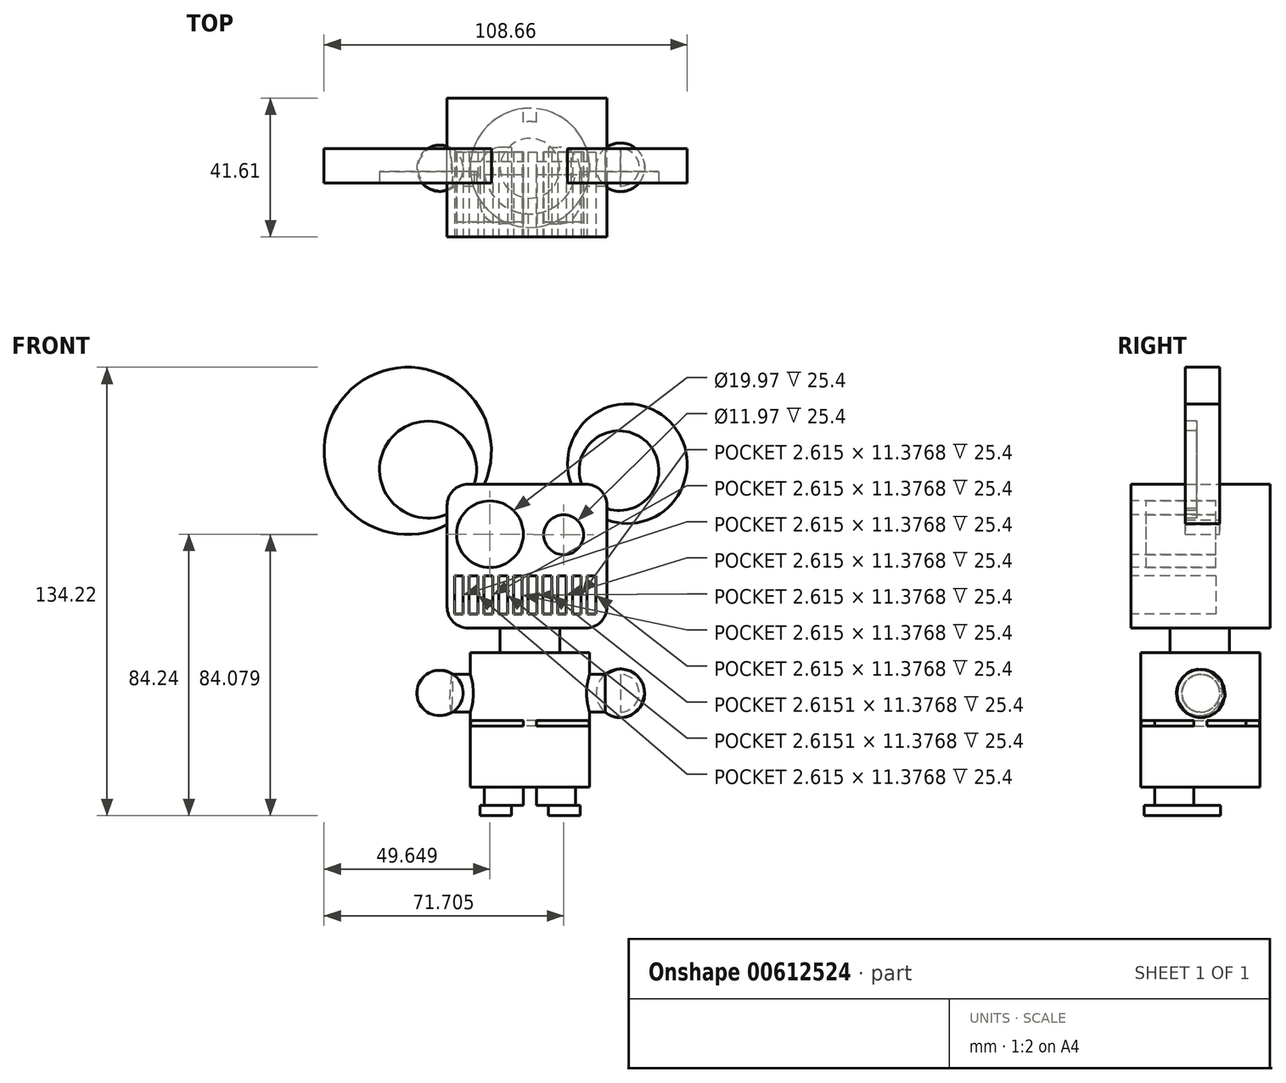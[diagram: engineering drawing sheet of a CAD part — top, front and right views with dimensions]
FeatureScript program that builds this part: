
annotation { "Feature Type Name" : "Feature", "Feature Type Description" : "" }
export const myFeature = defineFeature(function(context is Context, id is Id, definition is map)
    precondition{}
    {
        {
            var Q0;
            Q0=qCreatedBy(makeId("Front.planeOp"),FACE);
            var sketch = newSketch(context, id + "F0", { "sketchPlane" : qUnion([Q0])});
            skLineSegment(sketch, "E0.bottom", {"start": v(-18.42, 27.46) * mm, "end": v(16.7, 27.46) * mm});
            skLineSegment(sketch, "E0.top", {"start": v(-18.42, -15.66) * mm, "end": v(16.7, -15.66) * mm});
            skLineSegment(sketch, "E0.left", {"start": v(-24.77, 21.1) * mm, "end": v(-24.77, -9.3) * mm});
            skLineSegment(sketch, "E0.right", {"start": v(23.04, 21.1) * mm, "end": v(23.04, -9.3) * mm});
            skPoint(sketch, "E1.visualSharp", {"position": v(23.04, 27.46) * mm});
            skArc(sketch, "E1.filletArc", {"start": v(23.04, 21.1) * mm, "mid": v(21.18, 25.6) * mm, "end": v(16.7, 27.46) * mm});
            skPoint(sketch, "E2.visualSharp", {"position": v(23.04, -15.66) * mm});
            skArc(sketch, "E2.filletArc", {"start": v(16.7, -15.66) * mm, "mid": v(21.18, -13.8) * mm, "end": v(23.04, -9.3) * mm});
            skPoint(sketch, "E3.visualSharp", {"position": v(-24.77, 27.46) * mm});
            skArc(sketch, "E3.filletArc", {"start": v(-18.42, 27.46) * mm, "mid": v(-22.9, 25.6) * mm, "end": v(-24.77, 21.1) * mm});
            skPoint(sketch, "E4.visualSharp", {"position": v(-24.77, -15.66) * mm});
            skArc(sketch, "E4.filletArc", {"start": v(-24.77, -9.3) * mm, "mid": v(-22.9, -13.8) * mm, "end": v(-18.42, -15.66) * mm});
            skSolve(sketch);
        }
        {
            var Q0;
            Q0 = qSketchRegion(id + "F0", true);
            extrude(context, id + "F1", {"entities" : qUnion([Q0]), "depth" : 41.6 * mm, "offsetDistance" : 25.4 * mm});
        }
        {
            var Q0;
            Q0=makeQuery(id+"F1.opExtrude","CAP_FACE",FACE,{"disambiguationData":[OSD([sQuery(id+"F0.wireOp",EDGE,"E0.bottom"),sQuery(id+"F0.wireOp",EDGE,"E0.top"),sQuery(id+"F0.wireOp",EDGE,"E0.left"),sQuery(id+"F0.wireOp",EDGE,"E0.right"),sQuery(id+"F0.wireOp",EDGE,"E1.filletArc"),sQuery(id+"F0.wireOp",EDGE,"E2.filletArc"),sQuery(id+"F0.wireOp",EDGE,"E3.filletArc"),sQuery(id+"F0.wireOp",EDGE,"E4.filletArc")])],"isStart":false});
            var sketch = newSketch(context, id + "F2", { "sketchPlane" : qUnion([Q0])});
            skCircle(sketch, "E5", {"center": v(-11.95, 12.46) * mm, "radius": 9.98 * mm});
            skSolve(sketch);
        }
        {
            var Q0;
            Q0 = qSketchRegion(id + "F2", true);
            extrude(context, id + "F3", {"entities" : qUnion([Q0]), "operationType" : NewBodyOperationType.REMOVE, "oppositeDirection" : true, "depth" : 25.4 * mm, "offsetDistance" : 25.4 * mm});
        }
        {
            var Q0;
            Q0=makeQuery(id+"F1.opExtrude","CAP_FACE",FACE,{"disambiguationData":[OSD([sQuery(id+"F0.wireOp",EDGE,"E0.bottom"),sQuery(id+"F0.wireOp",EDGE,"E0.top"),sQuery(id+"F0.wireOp",EDGE,"E0.left"),sQuery(id+"F0.wireOp",EDGE,"E0.right"),sQuery(id+"F0.wireOp",EDGE,"E1.filletArc"),sQuery(id+"F0.wireOp",EDGE,"E2.filletArc"),sQuery(id+"F0.wireOp",EDGE,"E3.filletArc"),sQuery(id+"F0.wireOp",EDGE,"E4.filletArc")])],"isStart":false});
            var sketch = newSketch(context, id + "F4", { "sketchPlane" : qUnion([Q0])});
            skCircle(sketch, "E6", {"center": v(10.1, 12.3) * mm, "radius": 5.99 * mm});
            skSolve(sketch);
        }
        {
            var Q0;
            Q0 = qSketchRegion(id + "F4", true);
            extrude(context, id + "F5", {"entities" : qUnion([Q0]), "operationType" : NewBodyOperationType.REMOVE, "oppositeDirection" : true, "depth" : 25.4 * mm, "offsetDistance" : 25.4 * mm});
        }
        {
            var Q0;
            Q0=makeQuery(id+"F3.boolean.opBoolean","COPY",FACE,{"derivedFrom":makeQuery(id+"F3.opExtrude","CAP_FACE",FACE,{"disambiguationData":[OSD([sQuery(id+"F2.wireOp",EDGE,"E5")])],"isStart":false})});
            var Q1;
            Q1=makeQuery(id+"F5.boolean.opBoolean","COPY",FACE,{"derivedFrom":makeQuery(id+"F5.opExtrude","CAP_FACE",FACE,{"disambiguationData":[OSD([sQuery(id+"F4.wireOp",EDGE,"E6")])],"isStart":false})});
            extrude(context, id + "F6", {"entities" : qUnion([Q0, Q1]), "depth" : 20.91 * mm, "offsetDistance" : 25.4 * mm});
        }
        {
            var Q0;
            Q0=makeQuery(id+"F1.opExtrude","CAP_FACE",FACE,{"disambiguationData":[OSD([sQuery(id+"F0.wireOp",EDGE,"E0.bottom"),sQuery(id+"F0.wireOp",EDGE,"E0.top"),sQuery(id+"F0.wireOp",EDGE,"E0.left"),sQuery(id+"F0.wireOp",EDGE,"E0.right"),sQuery(id+"F0.wireOp",EDGE,"E1.filletArc"),sQuery(id+"F0.wireOp",EDGE,"E2.filletArc"),sQuery(id+"F0.wireOp",EDGE,"E3.filletArc"),sQuery(id+"F0.wireOp",EDGE,"E4.filletArc")])],"isStart":false});
            var sketch = newSketch(context, id + "F7", { "sketchPlane" : qUnion([Q0])});
            skLineSegment(sketch, "E7.bottom", {"start": v(-22.58, 0) * mm, "end": v(-19.97, 0) * mm});
            skLineSegment(sketch, "E7.top", {"start": v(-22.58, -11.38) * mm, "end": v(-19.97, -11.38) * mm});
            skLineSegment(sketch, "E7.left", {"start": v(-22.58, 0) * mm, "end": v(-22.58, -11.38) * mm});
            skLineSegment(sketch, "E7.right", {"start": v(-19.97, 0) * mm, "end": v(-19.97, -11.38) * mm});
            skLineSegment(sketch, "E8.1.0.0", {"start": v(-18.17, 0) * mm, "end": v(-15.55, 0) * mm});
            skLineSegment(sketch, "E8.1.0.1", {"start": v(-15.55, 0) * mm, "end": v(-15.55, -11.38) * mm});
            skLineSegment(sketch, "E8.1.0.2", {"start": v(-18.17, 0) * mm, "end": v(-18.17, -11.38) * mm});
            skLineSegment(sketch, "E8.1.0.3", {"start": v(-18.17, -11.38) * mm, "end": v(-15.55, -11.38) * mm});
            skLineSegment(sketch, "E8.2.0.0", {"start": v(-13.76, 0) * mm, "end": v(-11.14, 0) * mm});
            skLineSegment(sketch, "E8.2.0.1", {"start": v(-11.14, 0) * mm, "end": v(-11.14, -11.38) * mm});
            skLineSegment(sketch, "E8.2.0.2", {"start": v(-13.76, 0) * mm, "end": v(-13.76, -11.38) * mm});
            skLineSegment(sketch, "E8.2.0.3", {"start": v(-13.76, -11.38) * mm, "end": v(-11.14, -11.38) * mm});
            skLineSegment(sketch, "E8.3.0.0", {"start": v(-9.34, 0) * mm, "end": v(-6.73, 0) * mm});
            skLineSegment(sketch, "E8.3.0.1", {"start": v(-6.73, 0) * mm, "end": v(-6.73, -11.38) * mm});
            skLineSegment(sketch, "E8.3.0.2", {"start": v(-9.34, 0) * mm, "end": v(-9.34, -11.38) * mm});
            skLineSegment(sketch, "E8.3.0.3", {"start": v(-9.34, -11.38) * mm, "end": v(-6.73, -11.38) * mm});
            skLineSegment(sketch, "E8.4.0.0", {"start": v(-4.93, 0) * mm, "end": v(-2.32, 0) * mm});
            skLineSegment(sketch, "E8.4.0.1", {"start": v(-2.32, 0) * mm, "end": v(-2.32, -11.38) * mm});
            skLineSegment(sketch, "E8.4.0.2", {"start": v(-4.93, 0) * mm, "end": v(-4.93, -11.38) * mm});
            skLineSegment(sketch, "E8.4.0.3", {"start": v(-4.93, -11.38) * mm, "end": v(-2.32, -11.38) * mm});
            skLineSegment(sketch, "E8.5.0.0", {"start": v(-0.52, 0) * mm, "end": v(2.1, 0) * mm});
            skLineSegment(sketch, "E8.5.0.1", {"start": v(2.1, 0) * mm, "end": v(2.1, -11.38) * mm});
            skLineSegment(sketch, "E8.5.0.2", {"start": v(-0.52, 0) * mm, "end": v(-0.52, -11.38) * mm});
            skLineSegment(sketch, "E8.5.0.3", {"start": v(-0.52, -11.38) * mm, "end": v(2.1, -11.38) * mm});
            skLineSegment(sketch, "E8.6.0.0", {"start": v(3.9, 0) * mm, "end": v(6.5, 0) * mm});
            skLineSegment(sketch, "E8.6.0.1", {"start": v(6.5, 0) * mm, "end": v(6.5, -11.38) * mm});
            skLineSegment(sketch, "E8.6.0.2", {"start": v(3.9, 0) * mm, "end": v(3.9, -11.38) * mm});
            skLineSegment(sketch, "E8.6.0.3", {"start": v(3.9, -11.38) * mm, "end": v(6.5, -11.38) * mm});
            skLineSegment(sketch, "E8.7.0.0", {"start": v(8.3, 0) * mm, "end": v(10.92, 0) * mm});
            skLineSegment(sketch, "E8.7.0.1", {"start": v(10.92, 0) * mm, "end": v(10.92, -11.38) * mm});
            skLineSegment(sketch, "E8.7.0.2", {"start": v(8.3, 0) * mm, "end": v(8.3, -11.38) * mm});
            skLineSegment(sketch, "E8.7.0.3", {"start": v(8.3, -11.38) * mm, "end": v(10.92, -11.38) * mm});
            skLineSegment(sketch, "E8.8.0.0", {"start": v(12.72, 0) * mm, "end": v(15.33, 0) * mm});
            skLineSegment(sketch, "E8.8.0.1", {"start": v(15.33, 0) * mm, "end": v(15.33, -11.38) * mm});
            skLineSegment(sketch, "E8.8.0.2", {"start": v(12.72, 0) * mm, "end": v(12.72, -11.38) * mm});
            skLineSegment(sketch, "E8.8.0.3", {"start": v(12.72, -11.38) * mm, "end": v(15.33, -11.38) * mm});
            skLineSegment(sketch, "E8.9.0.0", {"start": v(17.13, 0) * mm, "end": v(19.74, 0) * mm});
            skLineSegment(sketch, "E8.9.0.1", {"start": v(19.74, 0) * mm, "end": v(19.74, -11.38) * mm});
            skLineSegment(sketch, "E8.9.0.2", {"start": v(17.13, 0) * mm, "end": v(17.13, -11.38) * mm});
            skLineSegment(sketch, "E8.9.0.3", {"start": v(17.13, -11.38) * mm, "end": v(19.74, -11.38) * mm});
            skLineSegment(sketch, "E8.direction1", {"start": v(-22.58, -11.38) * mm, "end": v(-18.17, -11.38) * mm, "construction": true});
            skSolve(sketch);
        }
        {
            var Q0;
            Q0=makeQuery(id+"F7.imprint","IMPRINT",FACE,{"disambiguationData":[TD([[makeQuery(id+"F7.imprint","IMPRINT",EDGE,{"derivedFrom":sQuery(id+"F7.wireOp",EDGE,"E8.8.0.0")}),-1.0]])]});
            var Q1;
            Q1=makeQuery(id+"F7.imprint","IMPRINT",FACE,{"disambiguationData":[TD([[makeQuery(id+"F7.imprint","IMPRINT",EDGE,{"derivedFrom":sQuery(id+"F7.wireOp",EDGE,"E8.4.0.0")}),-1.0]])]});
            var Q2;
            Q2=makeQuery(id+"F7.imprint","IMPRINT",FACE,{"disambiguationData":[TD([[makeQuery(id+"F7.imprint","IMPRINT",EDGE,{"derivedFrom":sQuery(id+"F7.wireOp",EDGE,"E8.5.0.0")}),-1.0]])]});
            var Q3;
            Q3=makeQuery(id+"F7.imprint","IMPRINT",FACE,{"disambiguationData":[TD([[makeQuery(id+"F7.imprint","IMPRINT",EDGE,{"derivedFrom":sQuery(id+"F7.wireOp",EDGE,"E8.7.0.0")}),-1.0]])]});
            var Q4;
            Q4=makeQuery(id+"F7.imprint","IMPRINT",FACE,{"disambiguationData":[TD([[makeQuery(id+"F7.imprint","IMPRINT",EDGE,{"derivedFrom":sQuery(id+"F7.wireOp",EDGE,"E7.bottom")}),-1.0]])]});
            var Q5;
            Q5=makeQuery(id+"F7.imprint","IMPRINT",FACE,{"disambiguationData":[TD([[makeQuery(id+"F7.imprint","IMPRINT",EDGE,{"derivedFrom":sQuery(id+"F7.wireOp",EDGE,"E8.9.0.0")}),-1.0]])]});
            var Q6;
            Q6=makeQuery(id+"F7.imprint","IMPRINT",FACE,{"disambiguationData":[TD([[makeQuery(id+"F7.imprint","IMPRINT",EDGE,{"derivedFrom":sQuery(id+"F7.wireOp",EDGE,"E8.6.0.0")}),-1.0]])]});
            var Q7;
            Q7=makeQuery(id+"F7.imprint","IMPRINT",FACE,{"disambiguationData":[TD([[makeQuery(id+"F7.imprint","IMPRINT",EDGE,{"derivedFrom":sQuery(id+"F7.wireOp",EDGE,"E8.3.0.0")}),-1.0]])]});
            var Q8;
            Q8=makeQuery(id+"F7.imprint","IMPRINT",FACE,{"disambiguationData":[TD([[makeQuery(id+"F7.imprint","IMPRINT",EDGE,{"derivedFrom":sQuery(id+"F7.wireOp",EDGE,"E8.1.0.0")}),-1.0]])]});
            var Q9;
            Q9=makeQuery(id+"F7.imprint","IMPRINT",FACE,{"disambiguationData":[TD([[makeQuery(id+"F7.imprint","IMPRINT",EDGE,{"derivedFrom":sQuery(id+"F7.wireOp",EDGE,"E8.2.0.0")}),-1.0]])]});
            extrude(context, id + "F8", {"entities" : qUnion([Q0, Q1, Q2, Q3, Q4, Q5, Q6, Q7, Q8, Q9]), "operationType" : NewBodyOperationType.REMOVE, "oppositeDirection" : true, "depth" : 25.4 * mm, "offsetDistance" : 25.4 * mm});
        }
        {
            var Q0;
            Q0=qCreatedBy(makeId("Front.planeOp"),FACE);
            var sketch = newSketch(context, id + "F9", { "sketchPlane" : qUnion([Q0])});
            skCircle(sketch, "E9", {"center": v(29.16, 33.58) * mm, "radius": 17.9 * mm});
            skCircle(sketch, "E10", {"center": v(-36.57, 37.41) * mm, "radius": 25.03 * mm});
            skSolve(sketch);
        }
        {
            var Q0;
            Q0=makeQuery(id+"F9.imprint","IMPRINT",FACE,{"disambiguationData":[TD([[makeQuery(id+"F9.imprint","IMPRINT",EDGE,{"derivedFrom":sQuery(id+"F9.wireOp",EDGE,"E10")}),1.0]])]});
            var Q1;
            Q1=makeQuery(id+"F9.imprint","IMPRINT",FACE,{"disambiguationData":[TD([[makeQuery(id+"F9.imprint","IMPRINT",EDGE,{"derivedFrom":sQuery(id+"F9.wireOp",EDGE,"E9")}),1.0]])]});
            extrude(context, id + "F10", {"entities" : qUnion([Q0, Q1]), "operationType" : NewBodyOperationType.ADD, "depth" : 25.4 * mm, "offsetDistance" : 25.4 * mm, "hasSecondDirection" : true, "secondDirectionOppositeDirection" : false, "secondDirectionDepth" : 15.12 * mm});
        }
        {
            var Q0;
            Q0=makeQuery(id+"F10.opExtrude","CAP_FACE",FACE,{"disambiguationData":[OSD([sQuery(id+"F9.wireOp",EDGE,"E10")])],"isStart":false});
            var sketch = newSketch(context, id + "F11", { "sketchPlane" : qUnion([Q0])});
            skCircle(sketch, "E11", {"center": v(-30.48, 31.8) * mm, "radius": 14.5 * mm});
            skSolve(sketch);
        }
        {
            var Q0;
            Q0=makeQuery(id+"F10.opExtrude","CAP_FACE",FACE,{"disambiguationData":[OSD([sQuery(id+"F9.wireOp",EDGE,"E9")])],"isStart":false});
            var sketch = newSketch(context, id + "F12", { "sketchPlane" : qUnion([Q0])});
            skCircle(sketch, "E12", {"center": v(26.66, 31.5) * mm, "radius": 11.92 * mm});
            skSolve(sketch);
        }
        {
            var Q0;
            {var subQ1=makeQuery(id+"F10.opExtrude","CAP_FACE",FACE,{"disambiguationData":[OSD([sQuery(id+"F9.wireOp",EDGE,"E10")])],"isStart":false});var subQ6=makeQuery(id+"F10.boolean.opBoolean","INTERSECT",EDGE,{"derivedFrom":[makeQuery(id+"F1.opExtrude","SWEPT_FACE",FACE,{"disambiguationData":[OSD([sQuery(id+"F0.wireOp",EDGE,"E3.filletArc")])]}),subQ1]});Q0=makeQuery(id+"F11.imprint","IMPRINT",FACE,{"disambiguationData":[TD([[makeQuery(id+"F11.imprint","IMPRINT",EDGE,{"derivedFrom":subQ6}),-1.0]])]});}
            var Q1;
            {var subQ1=makeQuery(id+"F10.opExtrude","CAP_FACE",FACE,{"disambiguationData":[OSD([sQuery(id+"F9.wireOp",EDGE,"E9")])],"isStart":false});var subQ6=makeQuery(id+"F10.boolean.opBoolean","INTERSECT",EDGE,{"derivedFrom":[makeQuery(id+"F1.opExtrude","SWEPT_FACE",FACE,{"disambiguationData":[OSD([sQuery(id+"F0.wireOp",EDGE,"E1.filletArc")])]}),subQ1]});Q1=makeQuery(id+"F12.imprint","IMPRINT",FACE,{"disambiguationData":[TD([[makeQuery(id+"F12.imprint","IMPRINT",EDGE,{"derivedFrom":subQ6}),-1.0]])]});}
            extrude(context, id + "F13", {"entities" : qUnion([Q0, Q1]), "operationType" : NewBodyOperationType.REMOVE, "oppositeDirection" : true, "depth" : 3.41 * mm, "offsetDistance" : 25.4 * mm});
        }
        {
            var Q0;
            Q0=makeQuery(id+"F1.opExtrude","SWEPT_FACE",FACE,{"disambiguationData":[OSD([sQuery(id+"F0.wireOp",EDGE,"E0.top")])]});
            var sketch = newSketch(context, id + "F14", { "sketchPlane" : qUnion([Q0])});
            skCircle(sketch, "E13", {"center": v(0, 21.05) * mm, "radius": 8.93 * mm});
            skSolve(sketch);
        }
        {
            var Q0;
            Q0=makeQuery(id+"F14.imprint","IMPRINT",FACE,{"disambiguationData":[TD([[makeQuery(id+"F14.imprint","IMPRINT",EDGE,{"derivedFrom":sQuery(id+"F14.wireOp",EDGE,"E13")}),1.0]])]});
            extrude(context, id + "F15", {"entities" : qUnion([Q0]), "operationType" : NewBodyOperationType.ADD, "depth" : 7.35 * mm, "offsetDistance" : 25.4 * mm});
        }
        {
            var Q0;
            Q0=makeQuery(id+"F15.opExtrude","CAP_FACE",FACE,{"disambiguationData":[OSD([sQuery(id+"F14.wireOp",EDGE,"E13")])],"isStart":false});
            var sketch = newSketch(context, id + "F16", { "sketchPlane" : qUnion([Q0])});
            skSolve(sketch);
        }
        {
            var Q0;
            Q0=makeQuery(id+"F16.imprint","IMPRINT",FACE,{"disambiguationData":[TD([[makeQuery(id+"F16.imprint","IMPRINT",EDGE,{"derivedFrom":makeQuery(id+"F15.opExtrude","CAP_EDGE",EDGE,{"disambiguationData":[OSD([sQuery(id+"F14.wireOp",EDGE,"E13")])],"isStart":false})}),1.0]])]});
            var sketch = newSketch(context, id + "F17", { "sketchPlane" : qUnion([Q0])});
            skCircle(sketch, "E14", {"center": v(0, 20.9) * mm, "radius": 17.84 * mm});
            skSolve(sketch);
        }
        {
            var Q0;
            Q0 = qSketchRegion(id + "F17", true);
            extrude(context, id + "F18", {"entities" : qUnion([Q0]), "operationType" : NewBodyOperationType.ADD, "depth" : 40.3 * mm, "offsetDistance" : 25.4 * mm});
        }
        {
            var Q0;
            Q0=qCreatedBy(makeId("Right.planeOp"),FACE);
            var sketch = newSketch(context, id + "F19", { "sketchPlane" : qUnion([Q0])});
            skCircle(sketch, "E15", {"center": v(-20.76, -35.16) * mm, "radius": 5.67 * mm});
            skSolve(sketch);
        }
        {
            var Q0;
            Q0 = qSketchRegion(id + "F19", true);
            extrude(context, id + "F20", {"entities" : qUnion([Q0]), "operationType" : NewBodyOperationType.ADD, "depth" : 27.1 * mm, "offsetDistance" : 25.4 * mm, "hasSecondDirection" : true, "secondDirectionOppositeDirection" : true, "secondDirectionDepth" : 26.94 * mm});
        }
        {
            var Q0;
            Q0=makeQuery(id+"F18.opExtrude","CAP_FACE",FACE,{"disambiguationData":[OSD([sQuery(id+"F17.wireOp",EDGE,"E14")])],"isStart":false});
            var sketch = newSketch(context, id + "F21", { "sketchPlane" : qUnion([Q0])});
            skCircle(sketch, "E16", {"center": v(0, 20.9) * mm, "radius": 13.8 * mm});
            skLineSegment(sketch, "E17.bottom", {"start": v(-2.02, 41.19) * mm, "end": v(2.02, 41.19) * mm});
            skLineSegment(sketch, "E17.top", {"start": v(-2.02, 0.6) * mm, "end": v(2.02, 0.6) * mm});
            skLineSegment(sketch, "E17.left", {"start": v(-2.02, 41.19) * mm, "end": v(-2.02, 0.6) * mm});
            skLineSegment(sketch, "E17.right", {"start": v(2.02, 41.19) * mm, "end": v(2.02, 0.6) * mm});
            skLineSegment(sketch, "E18.bottom", {"start": v(-21.1, 22.87) * mm, "end": v(21.1, 22.87) * mm});
            skLineSegment(sketch, "E18.top", {"start": v(-21.1, 18.92) * mm, "end": v(21.1, 18.92) * mm});
            skLineSegment(sketch, "E18.left", {"start": v(-21.1, 22.87) * mm, "end": v(-21.1, 18.92) * mm});
            skLineSegment(sketch, "E18.right", {"start": v(21.1, 22.87) * mm, "end": v(21.1, 18.92) * mm});
            skSolve(sketch);
        }
        {
            var Q0;
            {var subQ0=sQuery(id+"F21.wireOp",EDGE,"E18.bottom");var subQ1=sQuery(id+"F21.wireOp",EDGE,"E17.left");var subQ2=makeQuery(id+"F21.imprint","INTERSECT",VERTEX,{"derivedFrom":[subQ1,subQ0]});Q0=makeQuery(id+"F21.imprint","IMPRINT",FACE,{"disambiguationData":[TD([[makeQuery(id+"F21.imprint","IMPRINT",EDGE,{"disambiguationData":[TD([[subQ2,-1.0]])],"derivedFrom":subQ1}),1.0]])]});}
            var Q1;
            {var subQ0=sQuery(id+"F21.wireOp",EDGE,"E17.bottom");Q1=makeQuery(id+"F21.imprint","IMPRINT",FACE,{"disambiguationData":[TD([[makeQuery(id+"F21.imprint","IMPRINT",EDGE,{"derivedFrom":subQ0}),-1.0]])]});}
            var Q2;
            {var subQ0=sQuery(id+"F21.wireOp",EDGE,"E18.right");Q2=makeQuery(id+"F21.imprint","IMPRINT",FACE,{"disambiguationData":[TD([[makeQuery(id+"F21.imprint","IMPRINT",EDGE,{"derivedFrom":subQ0}),-1.0]])]});}
            var Q3;
            {var subQ0=sQuery(id+"F21.wireOp",EDGE,"E18.top");var subQ1=sQuery(id+"F21.wireOp",EDGE,"E16");var subQ2=makeQuery(id+"F21.imprint","INTERSECT",VERTEX,{"disambiguationData":[OD(0.0)],"derivedFrom":[subQ1,subQ0]});Q3=makeQuery(id+"F21.imprint","IMPRINT",FACE,{"disambiguationData":[TD([[makeQuery(id+"F21.imprint","IMPRINT",EDGE,{"disambiguationData":[TD([[subQ2,-1.0]])],"derivedFrom":subQ1}),1.0]])]});}
            var Q4;
            {var subQ0=sQuery(id+"F21.wireOp",EDGE,"E17.top");Q4=makeQuery(id+"F21.imprint","IMPRINT",FACE,{"disambiguationData":[TD([[makeQuery(id+"F21.imprint","IMPRINT",EDGE,{"derivedFrom":subQ0}),1.0]])]});}
            var Q5;
            {var subQ0=sQuery(id+"F21.wireOp",EDGE,"E17.left");var subQ1=sQuery(id+"F21.wireOp",EDGE,"E16");var subQ2=makeQuery(id+"F21.imprint","INTERSECT",VERTEX,{"disambiguationData":[OD(0.0)],"derivedFrom":[subQ1,subQ0]});Q5=makeQuery(id+"F21.imprint","IMPRINT",FACE,{"disambiguationData":[TD([[makeQuery(id+"F21.imprint","IMPRINT",EDGE,{"disambiguationData":[TD([[subQ2,-1.0]])],"derivedFrom":subQ1}),1.0]])]});}
            var Q6;
            {var subQ0=sQuery(id+"F21.wireOp",EDGE,"E18.left");Q6=makeQuery(id+"F21.imprint","IMPRINT",FACE,{"disambiguationData":[TD([[makeQuery(id+"F21.imprint","IMPRINT",EDGE,{"derivedFrom":subQ0}),1.0]])]});}
            var Q7;
            {var subQ0=sQuery(id+"F21.wireOp",EDGE,"E18.bottom");var subQ1=sQuery(id+"F21.wireOp",EDGE,"E16");var subQ2=makeQuery(id+"F21.imprint","INTERSECT",VERTEX,{"disambiguationData":[OD(1.0)],"derivedFrom":[subQ1,subQ0]});Q7=makeQuery(id+"F21.imprint","IMPRINT",FACE,{"disambiguationData":[TD([[makeQuery(id+"F21.imprint","IMPRINT",EDGE,{"disambiguationData":[TD([[subQ2,-1.0]])],"derivedFrom":subQ1}),1.0]])]});}
            var Q8;
            {var subQ0=sQuery(id+"F21.wireOp",EDGE,"E17.right");var subQ1=sQuery(id+"F21.wireOp",EDGE,"E16");var subQ2=makeQuery(id+"F21.imprint","INTERSECT",VERTEX,{"disambiguationData":[OD(1.0)],"derivedFrom":[subQ1,subQ0]});Q8=makeQuery(id+"F21.imprint","IMPRINT",FACE,{"disambiguationData":[TD([[makeQuery(id+"F21.imprint","IMPRINT",EDGE,{"disambiguationData":[TD([[subQ2,-1.0]])],"derivedFrom":subQ1}),1.0]])]});}
            var Q9;
            {var subQ0=sQuery(id+"F21.wireOp",EDGE,"E17.right");var subQ1=sQuery(id+"F21.wireOp",EDGE,"E16");var subQ2=makeQuery(id+"F21.imprint","INTERSECT",VERTEX,{"disambiguationData":[OD(0.0)],"derivedFrom":[subQ1,subQ0]});Q9=makeQuery(id+"F21.imprint","IMPRINT",FACE,{"disambiguationData":[TD([[makeQuery(id+"F21.imprint","IMPRINT",EDGE,{"disambiguationData":[TD([[subQ2,-1.0]])],"derivedFrom":subQ1}),1.0]])]});}
            var Q10;
            {var subQ0=sQuery(id+"F21.wireOp",EDGE,"E18.bottom");var subQ1=sQuery(id+"F21.wireOp",EDGE,"E16");var subQ2=makeQuery(id+"F21.imprint","INTERSECT",VERTEX,{"disambiguationData":[OD(0.0)],"derivedFrom":[subQ1,subQ0]});Q10=makeQuery(id+"F21.imprint","IMPRINT",FACE,{"disambiguationData":[TD([[makeQuery(id+"F21.imprint","IMPRINT",EDGE,{"disambiguationData":[TD([[subQ2,1.0]])],"derivedFrom":subQ1}),1.0]])]});}
            var Q11;
            {var subQ0=sQuery(id+"F21.wireOp",EDGE,"E17.left");var subQ1=sQuery(id+"F21.wireOp",EDGE,"E16");var subQ2=makeQuery(id+"F21.imprint","INTERSECT",VERTEX,{"disambiguationData":[OD(1.0)],"derivedFrom":[subQ1,subQ0]});Q11=makeQuery(id+"F21.imprint","IMPRINT",FACE,{"disambiguationData":[TD([[makeQuery(id+"F21.imprint","IMPRINT",EDGE,{"disambiguationData":[TD([[subQ2,-1.0]])],"derivedFrom":subQ1}),1.0]])]});}
            var Q12;
            {var subQ0=sQuery(id+"F21.wireOp",EDGE,"E17.right");var subQ1=sQuery(id+"F21.wireOp",EDGE,"E16");var subQ2=makeQuery(id+"F21.imprint","INTERSECT",VERTEX,{"disambiguationData":[OD(0.0)],"derivedFrom":[subQ1,subQ0]});Q12=makeQuery(id+"F21.imprint","IMPRINT",FACE,{"disambiguationData":[TD([[makeQuery(id+"F21.imprint","IMPRINT",EDGE,{"disambiguationData":[TD([[subQ2,1.0]])],"derivedFrom":subQ1}),1.0]])]});}
            var Q13;
            {var subQ0=sQuery(id+"F21.wireOp",EDGE,"E17.right");var subQ1=sQuery(id+"F21.wireOp",EDGE,"E16");var subQ2=makeQuery(id+"F21.imprint","INTERSECT",VERTEX,{"disambiguationData":[OD(0.0)],"derivedFrom":[subQ1,subQ0]});Q13=makeQuery(id+"F21.imprint","IMPRINT",FACE,{"disambiguationData":[TD([[makeQuery(id+"F21.imprint","IMPRINT",EDGE,{"disambiguationData":[TD([[subQ2,1.0]])],"derivedFrom":subQ1}),-1.0]])]});}
            var Q14;
            {var subQ0=sQuery(id+"F21.wireOp",EDGE,"E18.top");var subQ1=sQuery(id+"F21.wireOp",EDGE,"E16");var subQ2=makeQuery(id+"F21.imprint","INTERSECT",VERTEX,{"disambiguationData":[OD(0.0)],"derivedFrom":[subQ1,subQ0]});Q14=makeQuery(id+"F21.imprint","IMPRINT",FACE,{"disambiguationData":[TD([[makeQuery(id+"F21.imprint","IMPRINT",EDGE,{"disambiguationData":[TD([[subQ2,-1.0]])],"derivedFrom":subQ1}),-1.0]])]});}
            var Q15;
            {var subQ0=sQuery(id+"F21.wireOp",EDGE,"E17.left");var subQ1=sQuery(id+"F21.wireOp",EDGE,"E16");var subQ2=makeQuery(id+"F21.imprint","INTERSECT",VERTEX,{"disambiguationData":[OD(0.0)],"derivedFrom":[subQ1,subQ0]});Q15=makeQuery(id+"F21.imprint","IMPRINT",FACE,{"disambiguationData":[TD([[makeQuery(id+"F21.imprint","IMPRINT",EDGE,{"disambiguationData":[TD([[subQ2,-1.0]])],"derivedFrom":subQ1}),-1.0]])]});}
            var Q16;
            {var subQ0=sQuery(id+"F21.wireOp",EDGE,"E17.right");var subQ1=sQuery(id+"F21.wireOp",EDGE,"E16");var subQ2=makeQuery(id+"F21.imprint","INTERSECT",VERTEX,{"disambiguationData":[OD(1.0)],"derivedFrom":[subQ1,subQ0]});Q16=makeQuery(id+"F21.imprint","IMPRINT",FACE,{"disambiguationData":[TD([[makeQuery(id+"F21.imprint","IMPRINT",EDGE,{"disambiguationData":[TD([[subQ2,-1.0]])],"derivedFrom":subQ1}),-1.0]])]});}
            extrude(context, id + "F22", {"entities" : qUnion([Q0, Q1, Q2, Q3, Q4, Q5, Q6, Q7, Q8, Q9, Q10, Q11, Q12, Q13, Q14, Q15, Q16]), "operationType" : NewBodyOperationType.REMOVE, "oppositeDirection" : true, "depth" : 19.95 * mm, "offsetDistance" : 25.4 * mm, "hasSecondDirection" : true, "secondDirectionOppositeDirection" : true, "secondDirectionDepth" : 18.37 * mm});
        }
        {
            var Q0;
            Q0=makeQuery(id+"F20.opExtrude","CAP_FACE",FACE,{"disambiguationData":[OSD([sQuery(id+"F19.wireOp",EDGE,"E15")])],"isStart":true});
            var sketch = newSketch(context, id + "F23", { "sketchPlane" : qUnion([Q0])});
            skSolve(sketch);
        }
        {
            var Q0;
            Q0=makeQuery(id+"F20.opExtrude","CAP_FACE",FACE,{"disambiguationData":[OSD([sQuery(id+"F19.wireOp",EDGE,"E15")])],"isStart":false});
            var sketch = newSketch(context, id + "F24", { "sketchPlane" : qUnion([Q0])});
            skCircle(sketch, "E19", {"center": v(-20.76, -35.16) * mm, "radius": 7.28 * mm});
            skLineSegment(sketch, "E20", {"start": v(-20.74, -27.88) * mm, "end": v(-20.76, -42.44) * mm});
            skSolve(sketch);
        }
        {
            var Q0;
            {var subQ0=sQuery(id+"F24.wireOp",EDGE,"E20");var subQ1=sQuery(id+"F24.wireOp",EDGE,"E19");var subQ2=makeQuery(id+"F24.imprint","INTERSECT",VERTEX,{"disambiguationData":[OD(0.0)],"derivedFrom":[subQ1,subQ0]});Q0=makeQuery(id+"F24.imprint","IMPRINT",FACE,{"disambiguationData":[TD([[makeQuery(id+"F24.imprint","IMPRINT",EDGE,{"disambiguationData":[TD([[subQ2,1.0]])],"derivedFrom":subQ1}),1.0]])]});}
            var Q1;
            Q1=sQuery(id+"F24.wireOp",EDGE,"E20");
            revolve(context, id + "F25", {"operationType" : NewBodyOperationType.ADD, "entities" : qUnion([Q0]), "axis" : qUnion([Q1]), "revolveType" : RevolveType.FULL});
        }
        {
            var Q0;
            Q0=makeQuery(id+"F23.imprint","IMPRINT",FACE,{"disambiguationData":[TD([[makeQuery(id+"F23.imprint","IMPRINT",EDGE,{"derivedFrom":makeQuery(id+"F20.opExtrude","CAP_EDGE",EDGE,{"disambiguationData":[OSD([sQuery(id+"F19.wireOp",EDGE,"E15")])],"isStart":true})}),-1.0]])]});
            var sketch = newSketch(context, id + "F26", { "sketchPlane" : qUnion([Q0])});
            skCircle(sketch, "E21", {"center": v(20.88, -35.05) * mm, "radius": 6.78 * mm});
            skLineSegment(sketch, "E22", {"start": v(21.03, -28.27) * mm, "end": v(21.03, -41.83) * mm});
            skSolve(sketch);
        }
        {
            var Q0;
            {var subQ0=sQuery(id+"F26.wireOp",EDGE,"E22");var subQ1=sQuery(id+"F26.wireOp",EDGE,"E21");var subQ2=makeQuery(id+"F26.imprint","INTERSECT",VERTEX,{"disambiguationData":[OD(0.0)],"derivedFrom":[subQ1,subQ0]});Q0=makeQuery(id+"F26.imprint","IMPRINT",FACE,{"disambiguationData":[TD([[makeQuery(id+"F26.imprint","IMPRINT",EDGE,{"disambiguationData":[TD([[subQ2,1.0]])],"derivedFrom":subQ1}),1.0]])]});}
            var Q1;
            {var subQ0=sQuery(id+"F26.wireOp",EDGE,"E22");var subQ1=makeQuery(id+"F23.imprint","IMPRINT",EDGE,{"derivedFrom":makeQuery(id+"F20.opExtrude","CAP_EDGE",EDGE,{"disambiguationData":[OSD([sQuery(id+"F19.wireOp",EDGE,"E15")])],"isStart":true})});var subQ2=makeQuery(id+"F26.imprint","INTERSECT",VERTEX,{"disambiguationData":[OD(0.0)],"derivedFrom":[subQ1,subQ0]});Q1=makeQuery(id+"F26.imprint","IMPRINT",FACE,{"disambiguationData":[TD([[makeQuery(id+"F26.imprint","IMPRINT",EDGE,{"disambiguationData":[TD([[subQ2,-1.0]])],"derivedFrom":subQ0}),1.0]])]});}
            var Q2;
            Q2=sQuery(id+"F26.wireOp",EDGE,"E22");
            revolve(context, id + "F27", {"operationType" : NewBodyOperationType.ADD, "entities" : qUnion([Q0, Q1]), "axis" : qUnion([Q2]), "revolveType" : RevolveType.FULL});
        }
        {
            var Q0;
            {var subQ0=sQuery(id+"F21.wireOp",EDGE,"E18.bottom");var subQ1=sQuery(id+"F21.wireOp",EDGE,"E16");var subQ2=makeQuery(id+"F21.imprint","INTERSECT",VERTEX,{"disambiguationData":[OD(1.0)],"derivedFrom":[subQ1,subQ0]});Q0=makeQuery(id+"F21.imprint","IMPRINT",FACE,{"disambiguationData":[TD([[makeQuery(id+"F21.imprint","IMPRINT",EDGE,{"disambiguationData":[TD([[subQ2,-1.0]])],"derivedFrom":subQ1}),1.0]])]});}
            var Q1;
            {var subQ0=sQuery(id+"F21.wireOp",EDGE,"E18.bottom");var subQ1=sQuery(id+"F21.wireOp",EDGE,"E16");var subQ2=makeQuery(id+"F21.imprint","INTERSECT",VERTEX,{"disambiguationData":[OD(0.0)],"derivedFrom":[subQ1,subQ0]});Q1=makeQuery(id+"F21.imprint","IMPRINT",FACE,{"disambiguationData":[TD([[makeQuery(id+"F21.imprint","IMPRINT",EDGE,{"disambiguationData":[TD([[subQ2,1.0]])],"derivedFrom":subQ1}),1.0]])]});}
            var Q2;
            {var subQ0=sQuery(id+"F21.wireOp",EDGE,"E17.left");var subQ1=sQuery(id+"F21.wireOp",EDGE,"E16");var subQ2=makeQuery(id+"F21.imprint","INTERSECT",VERTEX,{"disambiguationData":[OD(0.0)],"derivedFrom":[subQ1,subQ0]});Q2=makeQuery(id+"F21.imprint","IMPRINT",FACE,{"disambiguationData":[TD([[makeQuery(id+"F21.imprint","IMPRINT",EDGE,{"disambiguationData":[TD([[subQ2,-1.0]])],"derivedFrom":subQ1}),1.0]])]});}
            var Q3;
            {var subQ0=sQuery(id+"F21.wireOp",EDGE,"E17.right");var subQ1=sQuery(id+"F21.wireOp",EDGE,"E16");var subQ2=makeQuery(id+"F21.imprint","INTERSECT",VERTEX,{"disambiguationData":[OD(0.0)],"derivedFrom":[subQ1,subQ0]});Q3=makeQuery(id+"F21.imprint","IMPRINT",FACE,{"disambiguationData":[TD([[makeQuery(id+"F21.imprint","IMPRINT",EDGE,{"disambiguationData":[TD([[subQ2,1.0]])],"derivedFrom":subQ1}),1.0]])]});}
            extrude(context, id + "F28", {"entities" : qUnion([Q0, Q1, Q2, Q3]), "operationType" : NewBodyOperationType.ADD, "depth" : 5.46 * mm, "offsetDistance" : 25.4 * mm});
        }
        {
            var Q0;
            Q0=makeQuery(id+"F28.opExtrude","CAP_FACE",FACE,{"disambiguationData":[OSD([sQuery(id+"F21.wireOp",EDGE,"E16"),sQuery(id+"F21.wireOp",EDGE,"E17.right"),sQuery(id+"F21.wireOp",EDGE,"E18.top")])],"isStart":false});
            var sketch = newSketch(context, id + "F29", { "sketchPlane" : qUnion([Q0])});
            skSolve(sketch);
        }
        {
            var Q0;
            {var subQ4=sQuery(id+"F21.wireOp",EDGE,"E17.right");Q0=makeQuery(id+"F29.imprint","IMPRINT",FACE,{"disambiguationData":[TD([[makeQuery(id+"F29.imprint","IMPRINT",EDGE,{"derivedFrom":makeQuery(id+"F28.opExtrude","CAP_EDGE",EDGE,{"disambiguationData":[OSD([subQ4])],"isStart":false})}),1.0]])]});}
            var sketch = newSketch(context, id + "F30", { "sketchPlane" : qUnion([Q0])});
            skLineSegment(sketch, "E23.bottom", {"start": v(5.5, 14.8) * mm, "end": v(8.64, 14.8) * mm});
            skLineSegment(sketch, "E23.top", {"start": v(5.5, 37.69) * mm, "end": v(8.64, 37.69) * mm});
            skLineSegment(sketch, "E23.left", {"start": v(5.5, 14.8) * mm, "end": v(5.5, 37.69) * mm});
            skLineSegment(sketch, "E23.right", {"start": v(14.99, 21.14) * mm, "end": v(14.99, 31.34) * mm});
            skLineSegment(sketch, "E24", {"start": v(0, 0) * mm, "end": v(0, 40.74) * mm});
            skLineSegment(sketch, "E25.MirrorCS", {"start": v(-5.5, 14.8) * mm, "end": v(-5.5, 37.69) * mm});
            skLineSegment(sketch, "E26.MirrorCS", {"start": v(-14.99, 21.14) * mm, "end": v(-14.99, 31.34) * mm});
            skLineSegment(sketch, "E27.MirrorCS", {"start": v(-5.5, 14.8) * mm, "end": v(-8.64, 14.8) * mm});
            skLineSegment(sketch, "E28.MirrorCS", {"start": v(-5.5, 37.69) * mm, "end": v(-8.64, 37.69) * mm});
            skPoint(sketch, "E29.visualSharp", {"position": v(-14.99, 37.69) * mm});
            skArc(sketch, "E29.filletArc", {"start": v(-8.64, 37.69) * mm, "mid": v(-13.13, 35.83) * mm, "end": v(-14.99, 31.34) * mm});
            skPoint(sketch, "E30.visualSharp", {"position": v(-14.99, 14.8) * mm});
            skArc(sketch, "E30.filletArc", {"start": v(-14.99, 21.14) * mm, "mid": v(-13.13, 16.65) * mm, "end": v(-8.64, 14.8) * mm});
            skPoint(sketch, "E31.visualSharp", {"position": v(14.99, 37.69) * mm});
            skArc(sketch, "E31.filletArc", {"start": v(14.99, 31.34) * mm, "mid": v(13.13, 35.83) * mm, "end": v(8.64, 37.69) * mm});
            skPoint(sketch, "E32.visualSharp", {"position": v(14.99, 14.8) * mm});
            skArc(sketch, "E32.filletArc", {"start": v(8.64, 14.8) * mm, "mid": v(13.13, 16.65) * mm, "end": v(14.99, 21.14) * mm});
            skSolve(sketch);
        }
        {
            var Q0;
            Q0 = qSketchRegion(id + "F30", true);
            extrude(context, id + "F31", {"entities" : qUnion([Q0]), "operationType" : NewBodyOperationType.ADD, "depth" : 3.02 * mm, "offsetDistance" : 25.4 * mm});
        }
    });
